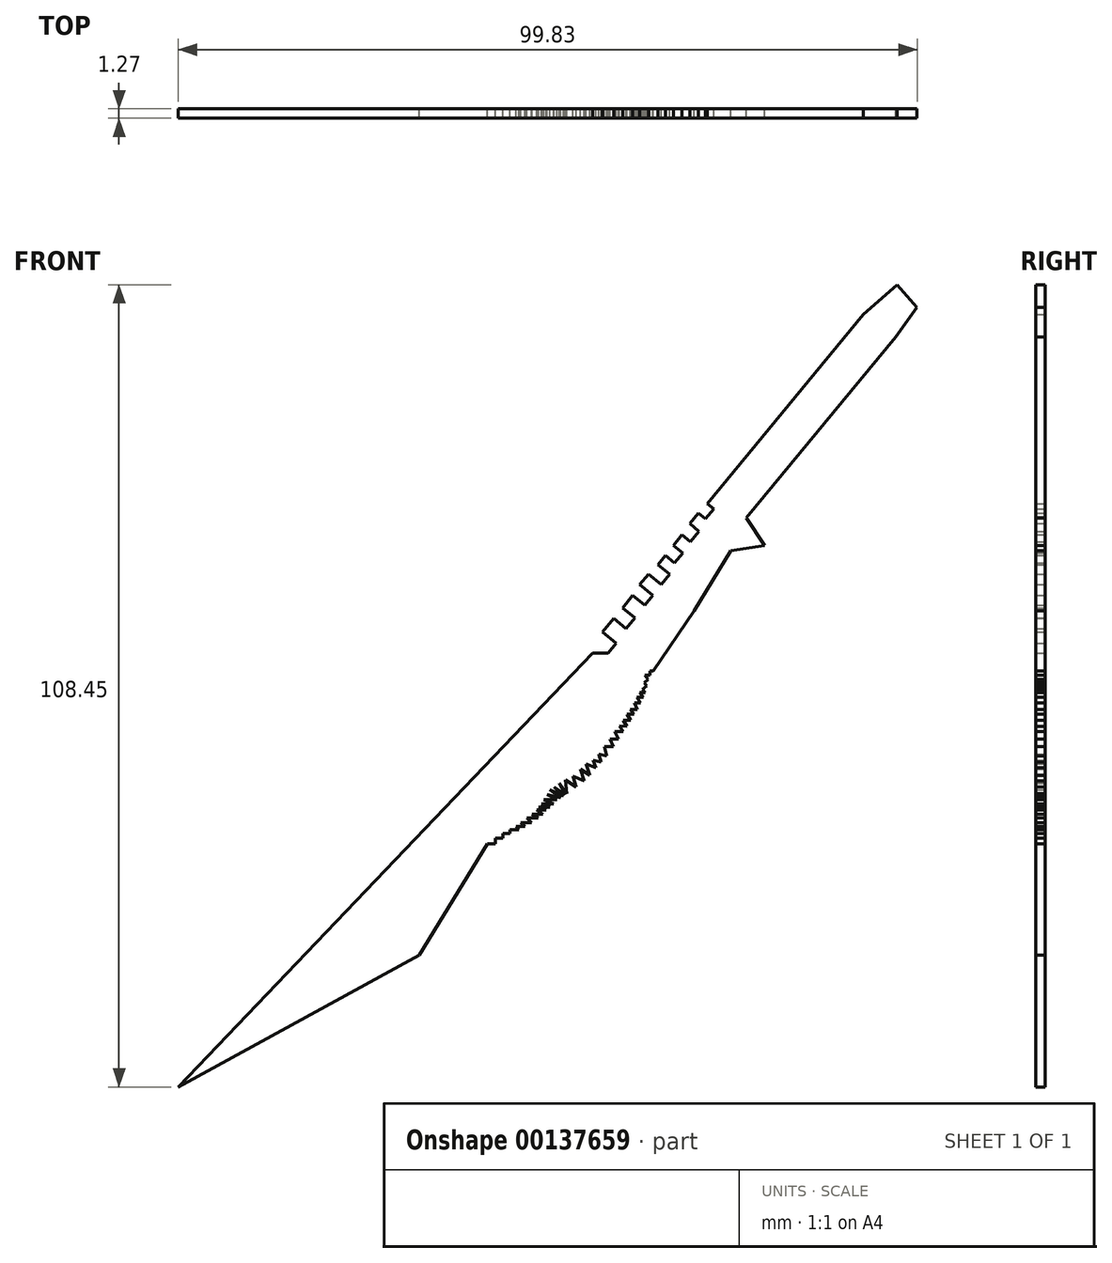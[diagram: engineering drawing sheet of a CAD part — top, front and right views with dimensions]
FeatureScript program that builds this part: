
annotation { "Feature Type Name" : "Feature", "Feature Type Description" : "" }
export const myFeature = defineFeature(function(context is Context, id is Id, definition is map)
    precondition{}
    {
        {
            var Q0;
            Q0=qCreatedBy(makeId("Front.planeOp"),FACE);
            var sketch = newSketch(context, id + "F0", { "sketchPlane" : qUnion([Q0])});
            skLineSegment(sketch, "E0", {"start": v(51.6, 61.2) * mm, "end": v(31.44, 36.72) * mm});
            skLineSegment(sketch, "E1", {"start": v(31.44, 36.72) * mm, "end": v(27.33, 40.1) * mm});
            skLineSegment(sketch, "E2", {"start": v(27.33, 40.1) * mm, "end": v(47.22, 64.24) * mm});
            skLineSegment(sketch, "E3", {"start": v(47.22, 64.24) * mm, "end": v(51.8, 68.26) * mm});
            skLineSegment(sketch, "E4", {"start": v(51.8, 68.26) * mm, "end": v(54.5, 65.17) * mm});
            skLineSegment(sketch, "E5", {"start": v(27.33, 40.1) * mm, "end": v(26.13, 38.65) * mm});
            skLineSegment(sketch, "E6", {"start": v(26.13, 38.65) * mm, "end": v(27.02, 37.93) * mm});
            skLineSegment(sketch, "E7", {"start": v(27.02, 37.93) * mm, "end": v(25.92, 36.6) * mm});
            skLineSegment(sketch, "E8", {"start": v(25.92, 36.6) * mm, "end": v(24.97, 37.39) * mm});
            skLineSegment(sketch, "E9", {"start": v(25, 34.88) * mm, "end": v(23.88, 33.53) * mm});
            skLineSegment(sketch, "E10", {"start": v(23.88, 33.53) * mm, "end": v(22.74, 34.47) * mm});
            skLineSegment(sketch, "E11", {"start": v(22.74, 34.47) * mm, "end": v(21.55, 33.03) * mm});
            skLineSegment(sketch, "E12", {"start": v(21.55, 33.03) * mm, "end": v(22.83, 31.98) * mm});
            skLineSegment(sketch, "E13", {"start": v(22.83, 31.98) * mm, "end": v(21.74, 30.65) * mm});
            skLineSegment(sketch, "E14", {"start": v(21.74, 30.65) * mm, "end": v(20.54, 31.64) * mm});
            skLineSegment(sketch, "E15", {"start": v(20.54, 31.64) * mm, "end": v(19.5, 30.38) * mm});
            skLineSegment(sketch, "E16", {"start": v(19.5, 30.38) * mm, "end": v(21.05, 29.1) * mm});
            skLineSegment(sketch, "E17", {"start": v(21.05, 29.1) * mm, "end": v(19.92, 27.72) * mm});
            skLineSegment(sketch, "E18", {"start": v(19.92, 27.72) * mm, "end": v(18.2, 29.14) * mm});
            skLineSegment(sketch, "E19", {"start": v(18.2, 29.14) * mm, "end": v(17.02, 27.7) * mm});
            skLineSegment(sketch, "E20", {"start": v(17.02, 27.7) * mm, "end": v(18.79, 26.25) * mm});
            skLineSegment(sketch, "E21", {"start": v(18.79, 26.25) * mm, "end": v(17.69, 24.92) * mm});
            skLineSegment(sketch, "E22", {"start": v(17.69, 24.92) * mm, "end": v(16.07, 26.25) * mm});
            skLineSegment(sketch, "E23", {"start": v(16.07, 26.25) * mm, "end": v(14.7, 24.59) * mm});
            skLineSegment(sketch, "E24", {"start": v(14.7, 24.59) * mm, "end": v(16.38, 23.2) * mm});
            skLineSegment(sketch, "E25", {"start": v(16.38, 23.2) * mm, "end": v(15.18, 21.74) * mm});
            skLineSegment(sketch, "E26", {"start": v(15.18, 21.74) * mm, "end": v(13.5, 23.13) * mm});
            skLineSegment(sketch, "E27", {"start": v(13.5, 23.13) * mm, "end": v(12, 21.31) * mm});
            skLineSegment(sketch, "E28", {"start": v(12, 21.31) * mm, "end": v(13.84, 19.8) * mm});
            skLineSegment(sketch, "E29", {"start": v(13.84, 19.8) * mm, "end": v(12.76, 18.48) * mm});
            skLineSegment(sketch, "E30", {"start": v(12.76, 18.48) * mm, "end": v(10.63, 18.48) * mm});
            skLineSegment(sketch, "E31", {"start": v(10.63, 18.48) * mm, "end": v(-45.32, -40.19) * mm});
            skLineSegment(sketch, "E32", {"start": v(-45.32, -40.19) * mm, "end": v(-12.74, -22.39) * mm});
            skLineSegment(sketch, "E33", {"start": v(-12.74, -22.39) * mm, "end": v(-4.1, -8.25) * mm});
            skLineSegment(sketch, "E34", {"start": v(24.97, 37.39) * mm, "end": v(23.8, 35.97) * mm});
            skLineSegment(sketch, "E35", {"start": v(23.8, 35.97) * mm, "end": v(25, 34.88) * mm});
            skLineSegment(sketch, "E36", {"start": v(-4.1, -8.25) * mm, "end": v(-3.55, -7.34) * mm});
            skLineSegment(sketch, "E37", {"start": v(31.44, 36.72) * mm, "end": v(33.9, 33.03) * mm});
            skLineSegment(sketch, "E38", {"start": v(33.9, 33.03) * mm, "end": v(29.33, 32.3) * mm});
            skLineSegment(sketch, "E39", {"start": v(29.33, 32.3) * mm, "end": v(24.36, 24.16) * mm});
            skLineSegment(sketch, "E40", {"start": v(24.36, 24.16) * mm, "end": v(18.87, 16.02) * mm});
            skLineSegment(sketch, "E41", {"start": v(-3.55, -7.34) * mm, "end": v(-2.5, -7.34) * mm});
            skLineSegment(sketch, "E42", {"start": v(-2.5, -7.34) * mm, "end": v(-2.5, -6.58) * mm});
            skLineSegment(sketch, "E43", {"start": v(-2.5, -6.58) * mm, "end": v(-1.47, -6.58) * mm});
            skLineSegment(sketch, "E44", {"start": v(-1.47, -6.58) * mm, "end": v(-1.47, -5.91) * mm});
            skLineSegment(sketch, "E45", {"start": v(-1.47, -5.91) * mm, "end": v(-0.49, -5.91) * mm});
            skLineSegment(sketch, "E46", {"start": v(18.87, 16.02) * mm, "end": v(18.4, 16.02) * mm});
            skLineSegment(sketch, "E47", {"start": v(18.4, 16.02) * mm, "end": v(18.4, 15.5) * mm});
            skLineSegment(sketch, "E48", {"start": v(18.4, 15.5) * mm, "end": v(17.7, 15.5) * mm});
            skLineSegment(sketch, "E49", {"start": v(17.7, 15.5) * mm, "end": v(18.17, 14.88) * mm});
            skLineSegment(sketch, "E50", {"start": v(18.17, 14.88) * mm, "end": v(17.61, 14.47) * mm});
            skLineSegment(sketch, "E51", {"start": v(17.61, 14.47) * mm, "end": v(17.95, 14.01) * mm});
            skLineSegment(sketch, "E52", {"start": v(17.95, 14.01) * mm, "end": v(17.4, 13.6) * mm});
            skLineSegment(sketch, "E53", {"start": v(17.4, 13.6) * mm, "end": v(17.77, 13.1) * mm});
            skLineSegment(sketch, "E54", {"start": v(17.77, 13.1) * mm, "end": v(17, 13.1) * mm});
            skLineSegment(sketch, "E55", {"start": v(17, 13.1) * mm, "end": v(17.5, 12.47) * mm});
            skLineSegment(sketch, "E56", {"start": v(17.5, 12.47) * mm, "end": v(16.65, 12.47) * mm});
            skLineSegment(sketch, "E57", {"start": v(16.65, 12.47) * mm, "end": v(17.12, 11.73) * mm});
            skLineSegment(sketch, "E58", {"start": v(17.12, 11.73) * mm, "end": v(16.34, 11.73) * mm});
            skLineSegment(sketch, "E59", {"start": v(16.34, 11.73) * mm, "end": v(16.7, 10.84) * mm});
            skLineSegment(sketch, "E60", {"start": v(16.7, 10.84) * mm, "end": v(15.72, 10.84) * mm});
            skLineSegment(sketch, "E61", {"start": v(15.72, 10.84) * mm, "end": v(16.22, 10.18) * mm});
            skLineSegment(sketch, "E62", {"start": v(-0.49, -5.91) * mm, "end": v(-0.49, -5.4) * mm});
            skLineSegment(sketch, "E63", {"start": v(-0.49, -5.4) * mm, "end": v(0.68, -5.4) * mm});
            skLineSegment(sketch, "E64", {"start": v(0.68, -5.4) * mm, "end": v(0.3, -4.99) * mm});
            skLineSegment(sketch, "E65", {"start": v(0.3, -4.99) * mm, "end": v(1.54, -4.99) * mm});
            skLineSegment(sketch, "E66", {"start": v(1.54, -4.99) * mm, "end": v(0.92, -4.44) * mm});
            skLineSegment(sketch, "E67", {"start": v(0.92, -4.44) * mm, "end": v(2.39, -4.44) * mm});
            skLineSegment(sketch, "E68", {"start": v(2.39, -4.44) * mm, "end": v(1.8, -3.85) * mm});
            skLineSegment(sketch, "E69", {"start": v(1.8, -3.85) * mm, "end": v(3.27, -3.85) * mm});
            skLineSegment(sketch, "E70", {"start": v(3.27, -3.85) * mm, "end": v(2.46, -3.3) * mm});
            skLineSegment(sketch, "E71", {"start": v(2.46, -3.3) * mm, "end": v(3.93, -3.3) * mm});
            skLineSegment(sketch, "E72", {"start": v(16.22, 10.18) * mm, "end": v(15.3, 10.18) * mm});
            skLineSegment(sketch, "E73", {"start": v(15.3, 10.18) * mm, "end": v(15.81, 9.4) * mm});
            skLineSegment(sketch, "E74", {"start": v(15.81, 9.4) * mm, "end": v(14.78, 9.4) * mm});
            skLineSegment(sketch, "E75", {"start": v(14.78, 9.4) * mm, "end": v(15.3, 8.58) * mm});
            skLineSegment(sketch, "E76", {"start": v(15.3, 8.58) * mm, "end": v(14.27, 8.62) * mm});
            skLineSegment(sketch, "E77", {"start": v(14.27, 8.62) * mm, "end": v(14.78, 7.89) * mm});
            skLineSegment(sketch, "E78", {"start": v(14.78, 7.89) * mm, "end": v(13.65, 7.89) * mm});
            skLineSegment(sketch, "E79", {"start": v(13.65, 7.89) * mm, "end": v(14.12, 6.86) * mm});
            skLineSegment(sketch, "E80", {"start": v(14.12, 6.86) * mm, "end": v(13.02, 6.86) * mm});
            skLineSegment(sketch, "E81", {"start": v(13.02, 6.86) * mm, "end": v(13.43, 5.8) * mm});
            skLineSegment(sketch, "E82", {"start": v(13.43, 5.8) * mm, "end": v(12.25, 5.8) * mm});
            skLineSegment(sketch, "E83", {"start": v(12.25, 5.8) * mm, "end": v(12.55, 4.58) * mm});
            skLineSegment(sketch, "E84", {"start": v(12.55, 4.58) * mm, "end": v(11.52, 4.8) * mm});
            skLineSegment(sketch, "E85", {"start": v(11.52, 4.8) * mm, "end": v(11.78, 3.74) * mm});
            skLineSegment(sketch, "E86", {"start": v(11.78, 3.74) * mm, "end": v(10.75, 4) * mm});
            skLineSegment(sketch, "E87", {"start": v(10.75, 4) * mm, "end": v(11.08, 2.93) * mm});
            skLineSegment(sketch, "E88", {"start": v(11.08, 2.93) * mm, "end": v(9.76, 3.45) * mm});
            skLineSegment(sketch, "E89", {"start": v(9.76, 3.45) * mm, "end": v(10.27, 1.98) * mm});
            skLineSegment(sketch, "E90", {"start": v(10.27, 1.98) * mm, "end": v(9.02, 2.79) * mm});
            skLineSegment(sketch, "E91", {"start": v(9.02, 2.79) * mm, "end": v(9.54, 1.17) * mm});
            skLineSegment(sketch, "E92", {"start": v(9.54, 1.17) * mm, "end": v(7.96, 1.85) * mm});
            skLineSegment(sketch, "E93", {"start": v(7.96, 1.85) * mm, "end": v(8.44, 0.34) * mm});
            skLineSegment(sketch, "E94", {"start": v(8.44, 0.34) * mm, "end": v(6.97, 1.3) * mm});
            skLineSegment(sketch, "E95", {"start": v(3.93, -3.3) * mm, "end": v(3.08, -2.73) * mm});
            skLineSegment(sketch, "E96", {"start": v(3.08, -2.73) * mm, "end": v(4.38, -2.73) * mm});
            skLineSegment(sketch, "E97", {"start": v(4.38, -2.73) * mm, "end": v(3.33, -2.34) * mm});
            skLineSegment(sketch, "E98", {"start": v(3.33, -2.34) * mm, "end": v(4.9, -2.34) * mm});
            skLineSegment(sketch, "E99", {"start": v(4.9, -2.34) * mm, "end": v(3.72, -1.92) * mm});
            skLineSegment(sketch, "E100", {"start": v(3.72, -1.92) * mm, "end": v(5.39, -1.92) * mm});
            skLineSegment(sketch, "E101", {"start": v(5.39, -1.92) * mm, "end": v(4.07, -1.37) * mm});
            skLineSegment(sketch, "E102", {"start": v(4.07, -1.37) * mm, "end": v(5.82, -1.37) * mm});
            skLineSegment(sketch, "E103", {"start": v(5.82, -1.37) * mm, "end": v(4.48, -0.65) * mm});
            skLineSegment(sketch, "E104", {"start": v(6.13, 0.9) * mm, "end": v(7.17, -0.56) * mm});
            skLineSegment(sketch, "E105", {"start": v(7.17, -0.56) * mm, "end": v(6.97, 1.3) * mm});
            skLineSegment(sketch, "E106", {"start": v(4.48, -0.65) * mm, "end": v(6.31, -1.1) * mm});
            skLineSegment(sketch, "E107", {"start": v(6.31, -1.1) * mm, "end": v(4.86, 0) * mm});
            skLineSegment(sketch, "E108", {"start": v(4.86, 0) * mm, "end": v(6.72, -0.83) * mm});
            skLineSegment(sketch, "E109", {"start": v(6.72, -0.83) * mm, "end": v(5.43, 0.34) * mm});
            skLineSegment(sketch, "E110", {"start": v(5.43, 0.34) * mm, "end": v(6.98, -0.68) * mm});
            skLineSegment(sketch, "E111", {"start": v(6.98, -0.68) * mm, "end": v(6.13, 0.9) * mm});
            skLineSegment(sketch, "E112", {"start": v(54.5, 65.17) * mm, "end": v(51.6, 61.2) * mm});
            skSolve(sketch);
        }
        {
            var Q0;
            Q0 = qSketchRegion(id + "F0", true);
            extrude(context, id + "F1", {"entities" : qUnion([Q0]), "depth" : 1.27 * mm});
        }
    });
